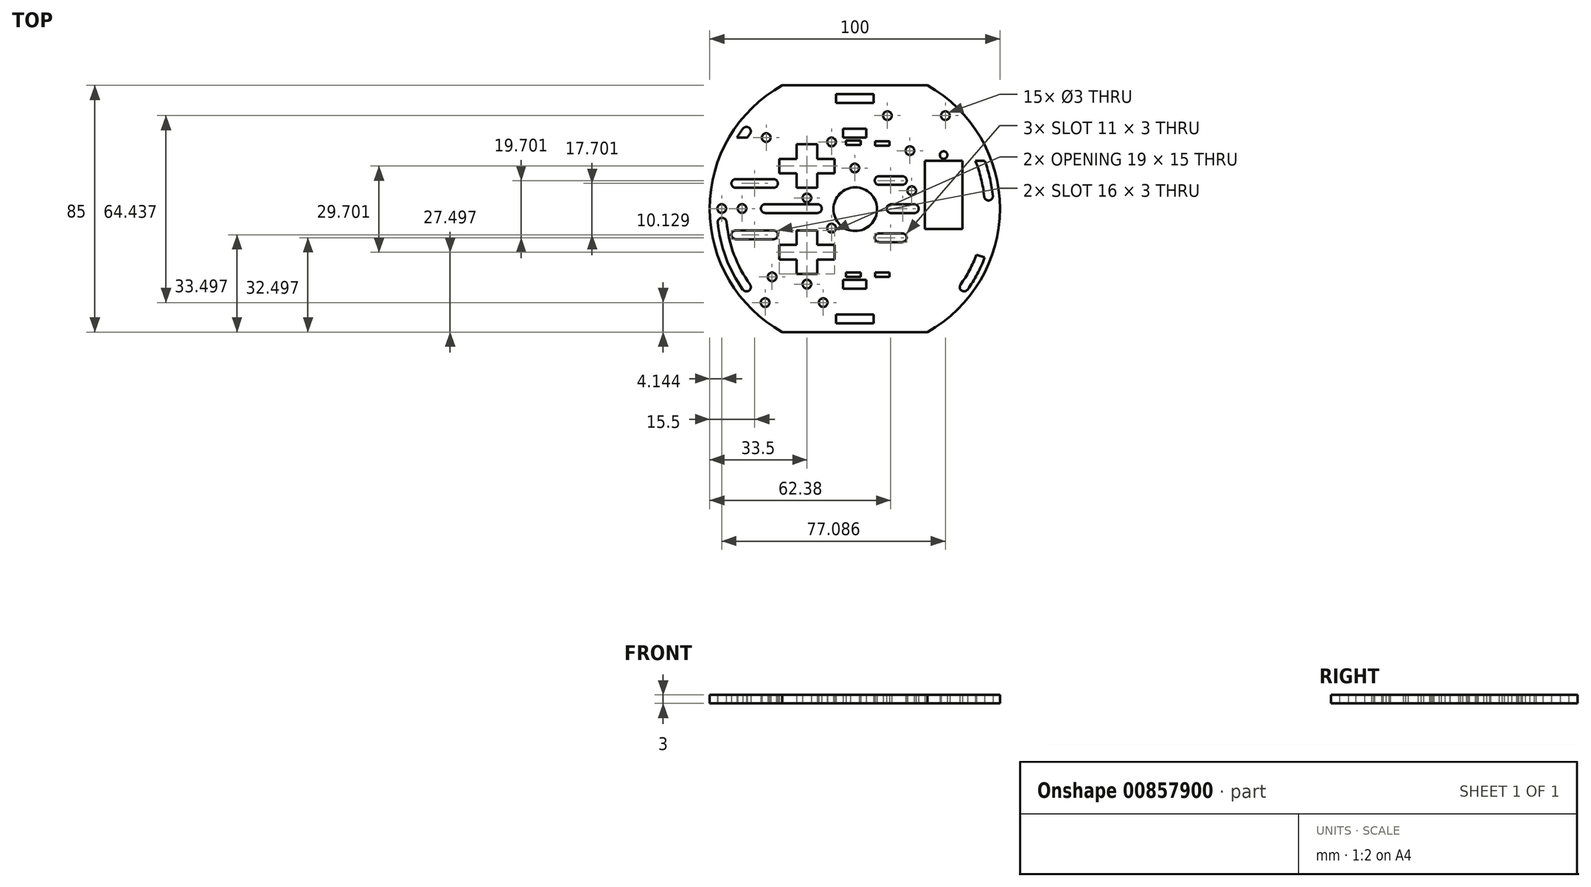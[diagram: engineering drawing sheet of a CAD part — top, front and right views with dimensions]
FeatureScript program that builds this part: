
annotation { "Feature Type Name" : "Feature", "Feature Type Description" : "" }
export const myFeature = defineFeature(function(context is Context, id is Id, definition is map)
    precondition{}
    {
        {
            var Q0;
            Q0=qCreatedBy(makeId("Top.planeOp"),FACE);
            var sketch = newSketch(context, id + "F0", { "sketchPlane" : qUnion([Q0])});
            skLineSegment(sketch, "E0", {"start": v(0, 43.49) * mm, "end": v(0, -41.51) * mm});
            skLineSegment(sketch, "E1.MirrorCS", {"start": v(0, -41.51) * mm, "end": v(25, -41.51) * mm});
            skLineSegment(sketch, "E2.MirrorCS", {"start": v(0, -41.51) * mm, "end": v(-25, -41.51) * mm});
            skLineSegment(sketch, "E3.MirrorCS", {"start": v(0, 43.49) * mm, "end": v(-25, 43.49) * mm});
            skLineSegment(sketch, "E4.MirrorCS", {"start": v(0, 43.49) * mm, "end": v(25, 43.49) * mm});
            skLineSegment(sketch, "E5", {"start": v(-50, 0.99) * mm, "end": v(0, 0.99) * mm});
            skPoint(sketch, "E5.startSnap0", {"position": v(0, 0.99) * mm});
            skLineSegment(sketch, "E6.MirrorCS", {"start": v(50, 0.99) * mm, "end": v(0, 0.99) * mm});
            skArc(sketch, "E7", {"start": v(-25, 43.49) * mm, "mid": v(-50, 0.99) * mm, "end": v(-25, -41.51) * mm});
            skArc(sketch, "E8.MirrorCS", {"start": v(25, 43.49) * mm, "mid": v(50, 0.99) * mm, "end": v(25, -41.51) * mm});
            skSolve(sketch);
        }
        {
            var Q0;
            {var subQ0=sQuery(id+"F0.wireOp",EDGE,"E4.MirrorCS");Q0=makeQuery(id+"F0.imprint","IMPRINT",FACE,{"disambiguationData":[TD([[makeQuery(id+"F0.imprint","IMPRINT",EDGE,{"derivedFrom":subQ0}),-1.0]])]});}
            var Q1;
            {var subQ0=sQuery(id+"F0.wireOp",EDGE,"E3.MirrorCS");Q1=makeQuery(id+"F0.imprint","IMPRINT",FACE,{"disambiguationData":[TD([[makeQuery(id+"F0.imprint","IMPRINT",EDGE,{"derivedFrom":subQ0}),1.0]])]});}
            var Q2;
            {var subQ0=sQuery(id+"F0.wireOp",EDGE,"E2.MirrorCS");Q2=makeQuery(id+"F0.imprint","IMPRINT",FACE,{"disambiguationData":[TD([[makeQuery(id+"F0.imprint","IMPRINT",EDGE,{"derivedFrom":subQ0}),-1.0]])]});}
            var Q3;
            {var subQ0=sQuery(id+"F0.wireOp",EDGE,"E1.MirrorCS");Q3=makeQuery(id+"F0.imprint","IMPRINT",FACE,{"disambiguationData":[TD([[makeQuery(id+"F0.imprint","IMPRINT",EDGE,{"derivedFrom":subQ0}),1.0]])]});}
            extrude(context, id + "F1", {"entities" : qUnion([Q0, Q1, Q2, Q3]), "depth" : 3 * mm, "offsetDistance" : 25.4 * mm});
        }
        {
            var Q0;
            Q0=qCreatedBy(makeId("Top.planeOp"),FACE);
            var sketch = newSketch(context, id + "F2", { "sketchPlane" : qUnion([Q0])});
            skLineSegment(sketch, "E9", {"start": v(-6.5, -38.51) * mm, "end": v(-6.5, -35.51) * mm});
            skLineSegment(sketch, "E10", {"start": v(-6.5, -35.51) * mm, "end": v(6.5, -35.51) * mm});
            skLineSegment(sketch, "E11", {"start": v(6.5, -35.51) * mm, "end": v(6.5, -38.51) * mm});
            skLineSegment(sketch, "E12", {"start": v(-6.5, -38.51) * mm, "end": v(6.5, -38.51) * mm});
            skCircle(sketch, "E13", {"center": v(0.17, 0.84) * mm, "radius": 7.5 * mm});
            skLineSegment(sketch, "E14", {"start": v(0, -26.51) * mm, "end": v(-4, -26.51) * mm});
            skLineSegment(sketch, "E15.MirrorCS", {"start": v(0, -26.51) * mm, "end": v(4, -26.51) * mm});
            skLineSegment(sketch, "E16", {"start": v(-4, -26.51) * mm, "end": v(-4, -23.51) * mm});
            skLineSegment(sketch, "E17", {"start": v(-4, -23.51) * mm, "end": v(4, -23.51) * mm});
            skLineSegment(sketch, "E18", {"start": v(4, -23.51) * mm, "end": v(4, -26.51) * mm});
            skLineSegment(sketch, "E19", {"start": v(-3, -22.51) * mm, "end": v(2, -22.51) * mm});
            skLineSegment(sketch, "E20", {"start": v(2, -22.51) * mm, "end": v(2, -21.01) * mm});
            skLineSegment(sketch, "E21", {"start": v(-3, -22.51) * mm, "end": v(-3, -21.01) * mm});
            skLineSegment(sketch, "E22", {"start": v(-3, -21.01) * mm, "end": v(2, -21.01) * mm});
            skLineSegment(sketch, "E23", {"start": v(37.11, 17.49) * mm, "end": v(37.11, -6.01) * mm});
            skLineSegment(sketch, "E24.MirrorCS", {"start": v(-6.5, 40.49) * mm, "end": v(6.5, 40.49) * mm});
            skLineSegment(sketch, "E25.MirrorCS", {"start": v(-6.5, 37.49) * mm, "end": v(6.5, 37.49) * mm});
            skLineSegment(sketch, "E26.MirrorCS", {"start": v(-6.5, 40.49) * mm, "end": v(-6.5, 37.49) * mm});
            skLineSegment(sketch, "E27.MirrorCS", {"start": v(6.5, 37.49) * mm, "end": v(6.5, 40.49) * mm});
            skLineSegment(sketch, "E28.MirrorCS", {"start": v(0, 28.49) * mm, "end": v(4, 28.49) * mm});
            skLineSegment(sketch, "E29.MirrorCS", {"start": v(0, 28.49) * mm, "end": v(-4, 28.49) * mm});
            skLineSegment(sketch, "E30.MirrorCS", {"start": v(-4, 28.49) * mm, "end": v(-4, 25.49) * mm});
            skLineSegment(sketch, "E31.MirrorCS", {"start": v(4, 25.49) * mm, "end": v(4, 28.49) * mm});
            skLineSegment(sketch, "E32.MirrorCS", {"start": v(-4, 25.49) * mm, "end": v(4, 25.49) * mm});
            skLineSegment(sketch, "E33.MirrorCS", {"start": v(-3, 24.49) * mm, "end": v(2, 24.49) * mm});
            skLineSegment(sketch, "E34.MirrorCS", {"start": v(-3, 24.49) * mm, "end": v(-3, 22.99) * mm});
            skLineSegment(sketch, "E35.MirrorCS", {"start": v(-3, 22.99) * mm, "end": v(2, 22.99) * mm});
            skLineSegment(sketch, "E36.MirrorCS", {"start": v(2, 24.49) * mm, "end": v(2, 22.99) * mm});
            skLineSegment(sketch, "E37", {"start": v(0, 43.49) * mm, "end": v(0, 40.49) * mm});
            skLineSegment(sketch, "E38", {"start": v(7, -21.01) * mm, "end": v(7, -22.51) * mm});
            skLineSegment(sketch, "E39", {"start": v(7, -21.01) * mm, "end": v(12, -21.01) * mm});
            skLineSegment(sketch, "E40", {"start": v(12, -21.01) * mm, "end": v(12, -22.51) * mm});
            skLineSegment(sketch, "E41", {"start": v(7, -22.51) * mm, "end": v(12, -22.51) * mm});
            skLineSegment(sketch, "E42", {"start": v(0.17, 0.84) * mm, "end": v(3.4, 0.84) * mm});
            skLineSegment(sketch, "E43.MirrorCS", {"start": v(7, 24.19) * mm, "end": v(12, 24.19) * mm});
            skLineSegment(sketch, "E44.MirrorCS", {"start": v(7, 22.69) * mm, "end": v(12, 22.69) * mm});
            skLineSegment(sketch, "E45.MirrorCS", {"start": v(7, 22.69) * mm, "end": v(7, 24.19) * mm});
            skLineSegment(sketch, "E46.MirrorCS", {"start": v(12, 22.69) * mm, "end": v(12, 24.19) * mm});
            skLineSegment(sketch, "E47", {"start": v(-25, -41.51) * mm, "end": v(-22, -41.51) * mm});
            skLineSegment(sketch, "E48", {"start": v(-20, -21.51) * mm, "end": v(-13, -21.51) * mm});
            skLineSegment(sketch, "E49", {"start": v(-20, -21.51) * mm, "end": v(-20, -16.51) * mm});
            skLineSegment(sketch, "E50", {"start": v(-20, -16.51) * mm, "end": v(-26, -16.51) * mm});
            skLineSegment(sketch, "E51", {"start": v(-26, -16.51) * mm, "end": v(-26, -11.51) * mm});
            skLineSegment(sketch, "E52", {"start": v(-26, -11.51) * mm, "end": v(-20, -11.51) * mm});
            skLineSegment(sketch, "E53", {"start": v(-20, -11.51) * mm, "end": v(-20, -6.51) * mm});
            skLineSegment(sketch, "E54", {"start": v(-20, -6.51) * mm, "end": v(-13, -6.51) * mm});
            skLineSegment(sketch, "E55", {"start": v(-13, -6.51) * mm, "end": v(-13, -11.51) * mm});
            skLineSegment(sketch, "E56", {"start": v(-13, -11.51) * mm, "end": v(-7, -11.51) * mm});
            skLineSegment(sketch, "E57", {"start": v(-7, -11.51) * mm, "end": v(-7, -16.51) * mm});
            skLineSegment(sketch, "E58", {"start": v(-7, -16.51) * mm, "end": v(-13, -16.51) * mm});
            skLineSegment(sketch, "E59", {"start": v(-13, -21.51) * mm, "end": v(-13, -16.51) * mm});
            skLineSegment(sketch, "E60.MirrorCS", {"start": v(-26, 13.19) * mm, "end": v(-20, 13.19) * mm});
            skLineSegment(sketch, "E61.MirrorCS", {"start": v(-26, 18.19) * mm, "end": v(-26, 13.19) * mm});
            skLineSegment(sketch, "E62.MirrorCS", {"start": v(-20, 18.19) * mm, "end": v(-26, 18.19) * mm});
            skLineSegment(sketch, "E63.MirrorCS", {"start": v(-20, 23.19) * mm, "end": v(-20, 18.19) * mm});
            skLineSegment(sketch, "E64.MirrorCS", {"start": v(-20, 23.19) * mm, "end": v(-13, 23.19) * mm});
            skLineSegment(sketch, "E65.MirrorCS", {"start": v(-13, 23.19) * mm, "end": v(-13, 18.19) * mm});
            skLineSegment(sketch, "E66.MirrorCS", {"start": v(-7, 18.19) * mm, "end": v(-13, 18.19) * mm});
            skLineSegment(sketch, "E67.MirrorCS", {"start": v(-7, 13.19) * mm, "end": v(-7, 18.19) * mm});
            skLineSegment(sketch, "E68.MirrorCS", {"start": v(-13, 13.19) * mm, "end": v(-7, 13.19) * mm});
            skLineSegment(sketch, "E69.MirrorCS", {"start": v(-13, 8.19) * mm, "end": v(-13, 13.19) * mm});
            skLineSegment(sketch, "E70.MirrorCS", {"start": v(-20, 8.19) * mm, "end": v(-13, 8.19) * mm});
            skLineSegment(sketch, "E71.MirrorCS", {"start": v(-20, 13.19) * mm, "end": v(-20, 8.19) * mm});
            skLineSegment(sketch, "E72", {"start": v(-28, -9.51) * mm, "end": v(-41, -9.51) * mm});
            skLineSegment(sketch, "E73", {"start": v(-41, -6.51) * mm, "end": v(-28, -6.51) * mm});
            skArc(sketch, "E74", {"start": v(-28, -6.51) * mm, "mid": v(-26.5, -8.01) * mm, "end": v(-28, -9.51) * mm});
            skArc(sketch, "E75", {"start": v(-41, -6.51) * mm, "mid": v(-42.5, -8.01) * mm, "end": v(-41, -9.51) * mm});
            skLineSegment(sketch, "E76.MirrorCS", {"start": v(-41, 8.19) * mm, "end": v(-28, 8.19) * mm});
            skArc(sketch, "E77.MirrorCS", {"start": v(-41, 8.19) * mm, "mid": v(-42.5, 9.69) * mm, "end": v(-41, 11.19) * mm});
            skLineSegment(sketch, "E78.MirrorCS", {"start": v(-28, 11.19) * mm, "end": v(-41, 11.19) * mm});
            skArc(sketch, "E79.MirrorCS", {"start": v(-28, 8.19) * mm, "mid": v(-26.5, 9.69) * mm, "end": v(-28, 11.19) * mm});
            skLineSegment(sketch, "E80", {"start": v(16.38, 12.19) * mm, "end": v(8.38, 12.19) * mm});
            skLineSegment(sketch, "E81", {"start": v(8.38, 9.19) * mm, "end": v(16.38, 9.19) * mm});
            skArc(sketch, "E82", {"start": v(8.38, 9.19) * mm, "mid": v(6.88, 10.69) * mm, "end": v(8.38, 12.19) * mm});
            skArc(sketch, "E83", {"start": v(16.38, 9.19) * mm, "mid": v(17.88, 10.69) * mm, "end": v(16.38, 12.19) * mm});
            skArc(sketch, "E84.MirrorCS", {"start": v(8.38, -7.51) * mm, "mid": v(6.88, -9.01) * mm, "end": v(8.38, -10.51) * mm});
            skArc(sketch, "E85.MirrorCS", {"start": v(16.38, -7.51) * mm, "mid": v(17.88, -9.01) * mm, "end": v(16.38, -10.51) * mm});
            skLineSegment(sketch, "E86", {"start": v(12.38, 43.49) * mm, "end": v(4.46, 43.49) * mm});
            skLineSegment(sketch, "E87", {"start": v(12.5, 2.49) * mm, "end": v(20.5, 2.49) * mm});
            skLineSegment(sketch, "E88", {"start": v(12.5, -0.51) * mm, "end": v(20.5, -0.51) * mm});
            skArc(sketch, "E89", {"start": v(12.5, 2.49) * mm, "mid": v(11, 0.99) * mm, "end": v(12.5, -0.51) * mm});
            skArc(sketch, "E90", {"start": v(20.5, -0.51) * mm, "mid": v(22, 0.99) * mm, "end": v(20.5, 2.49) * mm});
            skLineSegment(sketch, "E91", {"start": v(-12.86, 2.52) * mm, "end": v(-30.86, 2.52) * mm});
            skLineSegment(sketch, "E92", {"start": v(-30.4, 2.52) * mm, "end": v(-30.4, -0.48) * mm});
            skLineSegment(sketch, "E93", {"start": v(-30.86, -0.48) * mm, "end": v(-12.86, -0.48) * mm});
            skArc(sketch, "E94", {"start": v(-30.86, -0.48) * mm, "mid": v(-32.36, 1.02) * mm, "end": v(-30.86, 2.52) * mm});
            skArc(sketch, "E95", {"start": v(-12.86, -0.48) * mm, "mid": v(-11.36, 1.02) * mm, "end": v(-12.86, 2.52) * mm});
            skLineSegment(sketch, "E96.MirrorCS", {"start": v(16.38, -10.51) * mm, "end": v(8.38, -10.51) * mm});
            skLineSegment(sketch, "E97.MirrorCS", {"start": v(8.38, -7.51) * mm, "end": v(16.38, -7.51) * mm});
            skLineSegment(sketch, "E98", {"start": v(37.11, 17.49) * mm, "end": v(47.11, 17.49) * mm});
            skLineSegment(sketch, "E99", {"start": v(6.5, -38.51) * mm, "end": v(6.5, -41.51) * mm});
            skLineSegment(sketch, "E100", {"start": v(6.5, -41.51) * mm, "end": v(18.19, -41.51) * mm});
            skLineSegment(sketch, "E101", {"start": v(0, -35.51) * mm, "end": v(0, -37.8) * mm});
            skLineSegment(sketch, "E102", {"start": v(-13.99, -32.34) * mm, "end": v(-13.99, -41.51) * mm});
            skLineSegment(sketch, "E103", {"start": v(-13.99, -41.51) * mm, "end": v(-8.96, -41.51) * mm});
            skLineSegment(sketch, "E104", {"start": v(-12.39, -31.38) * mm, "end": v(-12.39, -37) * mm});
            skLineSegment(sketch, "E105", {"start": v(-12.39, -37) * mm, "end": v(-9.53, -37) * mm});
            skLineSegment(sketch, "E106", {"start": v(-29.39, -31.38) * mm, "end": v(-12.39, -31.38) * mm});
            skLineSegment(sketch, "E107", {"start": v(0.17, 0.84) * mm, "end": v(0.17, 6.05) * mm});
            skLineSegment(sketch, "E108", {"start": v(-16.5, 8.19) * mm, "end": v(-16.5, 6.19) * mm});
            skLineSegment(sketch, "E109", {"start": v(-26, 15.69) * mm, "end": v(-22.04, 15.69) * mm});
            skPoint(sketch, "E109.endSnap0", {"position": v(-7, 15.69) * mm});
            skLineSegment(sketch, "E110", {"start": v(-16.5, -21.51) * mm, "end": v(-16.5, -23.51) * mm});
            skLineSegment(sketch, "E111", {"start": v(-12.39, -31.38) * mm, "end": v(-10.89, -31.38) * mm});
            skCircle(sketch, "E112", {"center": v(-10.89, -31.38) * mm, "radius": 1.5 * mm});
            skLineSegment(sketch, "E113", {"start": v(-29.39, -31.38) * mm, "end": v(-30.89, -31.38) * mm});
            skCircle(sketch, "E114", {"center": v(-30.89, -31.38) * mm, "radius": 1.5 * mm});
            skCircle(sketch, "E115.MirrorC", {"center": v(31.23, -31.38) * mm, "radius": 1.5 * mm});
            skCircle(sketch, "E116.MirrorC", {"center": v(11.23, -31.38) * mm, "radius": 1.5 * mm});
            skCircle(sketch, "E117.MirrorC", {"center": v(11.23, 33.06) * mm, "radius": 1.5 * mm});
            skCircle(sketch, "E118.MirrorC", {"center": v(31.23, 33.06) * mm, "radius": 1.5 * mm});
            skCircle(sketch, "E119.MirrorC", {"center": v(-30.89, 33.06) * mm, "radius": 1.5 * mm});
            skCircle(sketch, "E120.MirrorC", {"center": v(-10.89, 33.06) * mm, "radius": 1.5 * mm});
            skLineSegment(sketch, "E121", {"start": v(-16.5, 6.19) * mm, "end": v(-16.5, 4.69) * mm});
            skCircle(sketch, "E122", {"center": v(-16.5, 4.69) * mm, "radius": 1.5 * mm});
            skCircle(sketch, "E123.MirrorC", {"center": v(-16.5, 26.69) * mm, "radius": 1.5 * mm});
            skCircle(sketch, "E124.MirrorC", {"center": v(-16.5, -3.01) * mm, "radius": 1.5 * mm});
            skCircle(sketch, "E125.MirrorC", {"center": v(-16.5, -25.01) * mm, "radius": 1.5 * mm});
            skLineSegment(sketch, "E126", {"start": v(-32.36, 1.02) * mm, "end": v(-37.36, 1.02) * mm});
            skLineSegment(sketch, "E127", {"start": v(-37.36, 1.02) * mm, "end": v(-38.86, 1.02) * mm});
            skCircle(sketch, "E128", {"center": v(-38.86, 1.02) * mm, "radius": 1.5 * mm});
            skLineSegment(sketch, "E129", {"start": v(-40.36, 1.02) * mm, "end": v(-44.36, 1.02) * mm});
            skLineSegment(sketch, "E130", {"start": v(-44.36, 1.02) * mm, "end": v(-45.86, 1.02) * mm});
            skCircle(sketch, "E131", {"center": v(-45.86, 1.02) * mm, "radius": 1.5 * mm});
            skCircle(sketch, "E132.MirrorC", {"center": v(39.2, 1.02) * mm, "radius": 1.5 * mm});
            skCircle(sketch, "E133.MirrorC", {"center": v(46.2, 1.02) * mm, "radius": 1.5 * mm});
            skLineSegment(sketch, "E134", {"start": v(24.11, 5.74) * mm, "end": v(28.02, 5.74) * mm});
            skLineSegment(sketch, "E135", {"start": v(24.11, 17.49) * mm, "end": v(37.11, 17.49) * mm});
            skLineSegment(sketch, "E136", {"start": v(37.11, -6.01) * mm, "end": v(24.11, -6.01) * mm});
            skLineSegment(sketch, "E137", {"start": v(30.61, 17.49) * mm, "end": v(30.61, 18.49) * mm});
            skLineSegment(sketch, "E138", {"start": v(30.61, 18.49) * mm, "end": v(30.61, 19.49) * mm});
            skCircle(sketch, "E139", {"center": v(30.61, 19.49) * mm, "radius": 1.3 * mm});
            skCircle(sketch, "E140.MirrorC", {"center": v(30.61, -8.01) * mm, "radius": 1.3 * mm});
            skLineSegment(sketch, "E141", {"start": v(25, 43.49) * mm, "end": v(19, 43.49) * mm});
            skLineSegment(sketch, "E142", {"start": v(19, 43.49) * mm, "end": v(19, 22.49) * mm});
            skLineSegment(sketch, "E143", {"start": v(19, 22.49) * mm, "end": v(19, 20.99) * mm});
            skCircle(sketch, "E144", {"center": v(19, 20.99) * mm, "radius": 1.5 * mm});
            skCircle(sketch, "E145.MirrorC", {"center": v(19, -19.31) * mm, "radius": 1.5 * mm});
            skLineSegment(sketch, "E146", {"start": v(-8, 43.49) * mm, "end": v(-8, 25.49) * mm});
            skLineSegment(sketch, "E147", {"start": v(-8, 25.49) * mm, "end": v(-8, 23.99) * mm});
            skCircle(sketch, "E148", {"center": v(-8, 23.99) * mm, "radius": 1.5 * mm});
            skCircle(sketch, "E149.MirrorC", {"center": v(-8, 7.39) * mm, "radius": 1.5 * mm});
            skCircle(sketch, "E150.MirrorC", {"center": v(-8, -5.71) * mm, "radius": 1.5 * mm});
            skCircle(sketch, "E151.MirrorC", {"center": v(-8, -22.31) * mm, "radius": 1.5 * mm});
            skLineSegment(sketch, "E152", {"start": v(25, 43.49) * mm, "end": v(0, 43.49) * mm});
            skLineSegment(sketch, "E153", {"start": v(0, 43.49) * mm, "end": v(0, 16.49) * mm});
            skLineSegment(sketch, "E154", {"start": v(0, 16.49) * mm, "end": v(0, 14.99) * mm});
            skCircle(sketch, "E155", {"center": v(0, 14.99) * mm, "radius": 1.5 * mm});
            skCircle(sketch, "E156.MirrorC", {"center": v(0, -13.31) * mm, "radius": 1.5 * mm});
            skLineSegment(sketch, "E157", {"start": v(-25, 43.49) * mm, "end": v(-21, 43.49) * mm});
            skLineSegment(sketch, "E158", {"start": v(-21, 43.49) * mm, "end": v(-21, 25.49) * mm});
            skLineSegment(sketch, "E159", {"start": v(-21, 25.49) * mm, "end": v(-29, 25.49) * mm});
            skLineSegment(sketch, "E160", {"start": v(-29, 25.49) * mm, "end": v(-30.5, 25.49) * mm});
            skCircle(sketch, "E161", {"center": v(-30.5, 25.49) * mm, "radius": 1.5 * mm});
            skLineSegment(sketch, "E162", {"start": v(-32, 25.49) * mm, "end": v(-43.38, 25.49) * mm});
            skLineSegment(sketch, "E163", {"start": v(-22, -41.51) * mm, "end": v(-22, -22.51) * mm});
            skLineSegment(sketch, "E164", {"start": v(-22, -22.51) * mm, "end": v(-27, -22.51) * mm});
            skLineSegment(sketch, "E165", {"start": v(-27, -22.51) * mm, "end": v(-28.5, -22.51) * mm});
            skCircle(sketch, "E166", {"center": v(-28.5, -22.51) * mm, "radius": 1.5 * mm});
            skLineSegment(sketch, "E167", {"start": v(24.11, 7.19) * mm, "end": v(21.11, 7.19) * mm});
            skLineSegment(sketch, "E168", {"start": v(21.11, 7.19) * mm, "end": v(19.61, 7.19) * mm});
            skCircle(sketch, "E169", {"center": v(19.61, 7.19) * mm, "radius": 1.5 * mm});
            skLineSegment(sketch, "E170", {"start": v(24.11, 17.49) * mm, "end": v(24.11, -6.01) * mm});
            skCircle(sketch, "E171.MirrorC", {"center": v(19.61, -5.51) * mm, "radius": 1.5 * mm});
            skArc(sketch, "E172", {"start": v(47.59, -3.52) * mm, "mid": v(44.79, -15.8) * mm, "end": v(38.88, -26.9) * mm});
            skArc(sketch, "E173", {"start": v(44.58, -3.52) * mm, "mid": v(41.94, -14.87) * mm, "end": v(36.45, -25.14) * mm});
            skArc(sketch, "E174", {"start": v(36.45, -25.14) * mm, "mid": v(36.79, -27.22) * mm, "end": v(38.88, -26.9) * mm});
            skArc(sketch, "E175", {"start": v(44.58, -3.52) * mm, "mid": v(46.08, -2.16) * mm, "end": v(47.59, -3.52) * mm});
            skLineSegment(sketch, "E176", {"start": v(41.94, -14.87) * mm, "end": v(44.79, -15.8) * mm});
            skArc(sketch, "E177.MirrorCS", {"start": v(-47.25, -3.52) * mm, "mid": v(-44.45, -15.8) * mm, "end": v(-38.53, -26.9) * mm});
            skArc(sketch, "E178.MirrorCS", {"start": v(-44.23, -3.52) * mm, "mid": v(-41.6, -14.87) * mm, "end": v(-36.1, -25.14) * mm});
            skArc(sketch, "E179.MirrorCS", {"start": v(-36.1, -25.14) * mm, "mid": v(-36.45, -27.22) * mm, "end": v(-38.53, -26.9) * mm});
            skArc(sketch, "E180.MirrorCS", {"start": v(-44.23, -3.52) * mm, "mid": v(-45.74, -2.16) * mm, "end": v(-47.25, -3.52) * mm});
            skArc(sketch, "E181.MirrorCS", {"start": v(44.58, 5.2) * mm, "mid": v(41.94, 16.54) * mm, "end": v(36.45, 26.81) * mm});
            skArc(sketch, "E182.MirrorCS", {"start": v(47.59, 5.2) * mm, "mid": v(44.79, 17.47) * mm, "end": v(38.88, 28.57) * mm});
            skArc(sketch, "E183.MirrorCS", {"start": v(44.58, 5.2) * mm, "mid": v(46.08, 3.83) * mm, "end": v(47.59, 5.2) * mm});
            skArc(sketch, "E184.MirrorCS", {"start": v(36.45, 26.81) * mm, "mid": v(36.79, 28.9) * mm, "end": v(38.88, 28.57) * mm});
            skArc(sketch, "E185.MirrorCS", {"start": v(-47.25, 5.2) * mm, "mid": v(-44.45, 17.47) * mm, "end": v(-38.53, 28.57) * mm});
            skArc(sketch, "E186.MirrorCS", {"start": v(-44.23, 5.2) * mm, "mid": v(-41.6, 16.54) * mm, "end": v(-36.1, 26.81) * mm});
            skArc(sketch, "E187.MirrorCS", {"start": v(-36.1, 26.81) * mm, "mid": v(-36.45, 28.9) * mm, "end": v(-38.53, 28.57) * mm});
            skArc(sketch, "E188.MirrorCS", {"start": v(-44.23, 5.2) * mm, "mid": v(-45.74, 3.83) * mm, "end": v(-47.25, 5.2) * mm});
            skSolve(sketch);
        }
        {
            var Q0;
            Q0=makeQuery(id+"F2.imprint","IMPRINT",FACE,{"disambiguationData":[TD([[makeQuery(id+"F2.imprint","IMPRINT",EDGE,{"derivedFrom":sQuery(id+"F2.wireOp",EDGE,"2JhbG11d-Ylxn-ed14-tFHQ-MPQ8VMmL4TC8")}),1.0]])]});
            var Q1;
            Q1=makeQuery(id+"F2.imprint","IMPRINT",FACE,{"disambiguationData":[TD([[makeQuery(id+"F2.imprint","IMPRINT",EDGE,{"derivedFrom":sQuery(id+"F2.wireOp",EDGE,"E13")}),1.0]])]});
            var Q2;
            Q2=makeQuery(id+"F2.imprint","IMPRINT",FACE,{"disambiguationData":[TD([[makeQuery(id+"F2.imprint","IMPRINT",EDGE,{"derivedFrom":sQuery(id+"F2.wireOp",EDGE,"E60.MirrorCS")}),1.0]])]});
            var Q3;
            Q3=makeQuery(id+"F2.imprint","IMPRINT",FACE,{"disambiguationData":[TD([[makeQuery(id+"F2.imprint","IMPRINT",EDGE,{"derivedFrom":sQuery(id+"F2.wireOp",EDGE,"E25.MirrorCS")}),1.0]])]});
            var Q4;
            Q4=makeQuery(id+"F2.imprint","IMPRINT",FACE,{"disambiguationData":[TD([[makeQuery(id+"F2.imprint","IMPRINT",EDGE,{"derivedFrom":sQuery(id+"F2.wireOp",EDGE,"E48")}),1.0]])]});
            var Q5;
            Q5=makeQuery(id+"F2.imprint","IMPRINT",FACE,{"disambiguationData":[TD([[makeQuery(id+"F2.imprint","IMPRINT",EDGE,{"derivedFrom":sQuery(id+"F2.wireOp",EDGE,"E19")}),1.0]])]});
            extrude(context, id + "F3", {"entities" : qUnion([Q0, Q1, Q2, Q3, Q4, Q5]), "operationType" : NewBodyOperationType.REMOVE, "oppositeDirection" : true, "depth" : 25.4 * mm, "offsetDistance" : 25.4 * mm});
        }
        {
            var Q0;
            Q0=makeQuery(id+"F2.imprint","IMPRINT",FACE,{"disambiguationData":[TD([[makeQuery(id+"F2.imprint","IMPRINT",EDGE,{"derivedFrom":sQuery(id+"F2.wireOp",EDGE,"E28.MirrorCS")}),-1.0]])]});
            var Q1;
            Q1=makeQuery(id+"F2.imprint","IMPRINT",FACE,{"disambiguationData":[TD([[makeQuery(id+"F2.imprint","IMPRINT",EDGE,{"derivedFrom":sQuery(id+"F2.wireOp",EDGE,"E19")}),1.0]])]});
            var Q2;
            Q2=makeQuery(id+"F2.imprint","IMPRINT",FACE,{"disambiguationData":[TD([[makeQuery(id+"F2.imprint","IMPRINT",EDGE,{"derivedFrom":sQuery(id+"F2.wireOp",EDGE,"E38")}),1.0]])]});
            var Q3;
            Q3=makeQuery(id+"F2.imprint","IMPRINT",FACE,{"disambiguationData":[TD([[makeQuery(id+"F2.imprint","IMPRINT",EDGE,{"derivedFrom":sQuery(id+"F2.wireOp",EDGE,"E9")}),-1.0]])]});
            var Q4;
            Q4=makeQuery(id+"F2.imprint","IMPRINT",FACE,{"disambiguationData":[TD([[makeQuery(id+"F2.imprint","IMPRINT",EDGE,{"derivedFrom":sQuery(id+"F2.wireOp",EDGE,"E33.MirrorCS")}),-1.0]])]});
            var Q5;
            Q5=makeQuery(id+"F2.imprint","IMPRINT",FACE,{"disambiguationData":[TD([[makeQuery(id+"F2.imprint","IMPRINT",EDGE,{"derivedFrom":sQuery(id+"F2.wireOp",EDGE,"E14")}),-1.0]])]});
            var Q6;
            Q6=makeQuery(id+"F2.imprint","IMPRINT",FACE,{"disambiguationData":[TD([[makeQuery(id+"F2.imprint","IMPRINT",EDGE,{"derivedFrom":sQuery(id+"F2.wireOp",EDGE,"E43.MirrorCS")}),-1.0]])]});
            extrude(context, id + "F4", {"entities" : qUnion([Q0, Q1, Q2, Q3, Q4, Q5, Q6]), "operationType" : NewBodyOperationType.REMOVE, "oppositeDirection" : true, "depth" : 25.4 * mm, "offsetDistance" : 25.4 * mm});
        }
        {
            var Q0;
            Q0=makeQuery(id+"F2.imprint","IMPRINT",FACE,{"disambiguationData":[TD([[makeQuery(id+"F2.imprint","IMPRINT",EDGE,{"derivedFrom":sQuery(id+"F2.wireOp",EDGE,"E177.MirrorCS")}),1.0]])]});
            var Q1;
            {var subQ0=sQuery(id+"F2.wireOp",EDGE,"E128");var subQ1=makeQuery(id+"F2.imprint","IMPRINT",VERTEX,{"disambiguationData":[OD(0.0)],"derivedFrom":subQ0});Q1=makeQuery(id+"F2.imprint","IMPRINT",FACE,{"disambiguationData":[TD([[makeQuery(id+"F2.imprint","IMPRINT",EDGE,{"disambiguationData":[TD([[subQ1,-1.0]])],"derivedFrom":subQ0}),1.0]])]});}
            var Q2;
            Q2=makeQuery(id+"F2.imprint","IMPRINT",FACE,{"disambiguationData":[TD([[makeQuery(id+"F2.imprint","IMPRINT",EDGE,{"derivedFrom":sQuery(id+"F2.wireOp",EDGE,"E122")}),1.0]])]});
            var Q3;
            Q3=makeQuery(id+"F2.imprint","IMPRINT",FACE,{"disambiguationData":[TD([[makeQuery(id+"F2.imprint","IMPRINT",EDGE,{"derivedFrom":sQuery(id+"F2.wireOp",EDGE,"E144")}),1.0]])]});
            extrude(context, id + "F5", {"entities" : qUnion([Q0, Q1, Q2, Q3]), "operationType" : NewBodyOperationType.REMOVE, "oppositeDirection" : true, "depth" : 25.4 * mm, "offsetDistance" : 25.4 * mm});
        }
        {
            var Q0;
            {var subQ0=sQuery(id+"F2.wireOp",EDGE,"E174");Q0=makeQuery(id+"F2.imprint","IMPRINT",FACE,{"disambiguationData":[TD([[makeQuery(id+"F2.imprint","IMPRINT",EDGE,{"derivedFrom":subQ0}),1.0]])]});}
            var Q1;
            {var subQ0=sQuery(id+"F2.wireOp",EDGE,"E175");Q1=makeQuery(id+"F2.imprint","IMPRINT",FACE,{"disambiguationData":[TD([[makeQuery(id+"F2.imprint","IMPRINT",EDGE,{"derivedFrom":subQ0}),-1.0]])]});}
            extrude(context, id + "F6", {"entities" : qUnion([Q0, Q1]), "operationType" : NewBodyOperationType.REMOVE, "oppositeDirection" : true, "depth" : 25.4 * mm, "offsetDistance" : 25.4 * mm});
        }
        {
            var Q0;
            {var subQ2=sQuery(id+"F2.wireOp",EDGE,"E23");Q0=makeQuery(id+"F2.imprint","IMPRINT",FACE,{"disambiguationData":[TD([[makeQuery(id+"F2.imprint","IMPRINT",EDGE,{"derivedFrom":subQ2}),-1.0]])]});}
            var Q1;
            Q1=makeQuery(id+"F2.imprint","IMPRINT",FACE,{"disambiguationData":[TD([[makeQuery(id+"F2.imprint","IMPRINT",EDGE,{"derivedFrom":sQuery(id+"F2.wireOp",EDGE,"E13")}),1.0]])]});
            var Q2;
            {var subQ2=sQuery(id+"F2.wireOp",EDGE,"E92");Q2=makeQuery(id+"F2.imprint","IMPRINT",FACE,{"disambiguationData":[TD([[makeQuery(id+"F2.imprint","IMPRINT",EDGE,{"derivedFrom":subQ2}),1.0]])]});}
            var Q3;
            {var subQ0=sQuery(id+"F2.wireOp",EDGE,"E60.MirrorCS");Q3=makeQuery(id+"F2.imprint","IMPRINT",FACE,{"disambiguationData":[TD([[makeQuery(id+"F2.imprint","IMPRINT",EDGE,{"derivedFrom":subQ0}),1.0]])]});}
            var Q4;
            Q4=makeQuery(id+"F2.imprint","IMPRINT",FACE,{"disambiguationData":[TD([[makeQuery(id+"F2.imprint","IMPRINT",EDGE,{"derivedFrom":sQuery(id+"F2.wireOp",EDGE,"E76.MirrorCS")}),1.0]])]});
            var Q5;
            {var subQ0=sQuery(id+"F2.wireOp",EDGE,"E174");Q5=makeQuery(id+"F2.imprint","IMPRINT",FACE,{"disambiguationData":[TD([[makeQuery(id+"F2.imprint","IMPRINT",EDGE,{"derivedFrom":subQ0}),1.0]])]});}
            var Q6;
            {var subQ0=sQuery(id+"F2.wireOp",EDGE,"E175");Q6=makeQuery(id+"F2.imprint","IMPRINT",FACE,{"disambiguationData":[TD([[makeQuery(id+"F2.imprint","IMPRINT",EDGE,{"derivedFrom":subQ0}),-1.0]])]});}
            var Q7;
            Q7=makeQuery(id+"F2.imprint","IMPRINT",FACE,{"disambiguationData":[TD([[makeQuery(id+"F2.imprint","IMPRINT",EDGE,{"derivedFrom":sQuery(id+"F2.wireOp",EDGE,"E133.MirrorC")}),-1.0]])]});
            var Q8;
            Q8=makeQuery(id+"F2.imprint","IMPRINT",FACE,{"disambiguationData":[TD([[makeQuery(id+"F2.imprint","IMPRINT",EDGE,{"derivedFrom":sQuery(id+"F2.wireOp",EDGE,"E132.MirrorC")}),-1.0]])]});
            var Q9;
            {var subQ5=sQuery(id+"F2.wireOp",EDGE,"E183.MirrorCS");Q9=makeQuery(id+"F2.imprint","IMPRINT",FACE,{"disambiguationData":[TD([[makeQuery(id+"F2.imprint","IMPRINT",EDGE,{"derivedFrom":subQ5}),1.0]])]});}
            var Q10;
            {var subQ5=sQuery(id+"F2.wireOp",EDGE,"E184.MirrorCS");Q10=makeQuery(id+"F2.imprint","IMPRINT",FACE,{"disambiguationData":[TD([[makeQuery(id+"F2.imprint","IMPRINT",EDGE,{"derivedFrom":subQ5}),-1.0]])]});}
            var Q11;
            Q11=makeQuery(id+"F2.imprint","IMPRINT",FACE,{"disambiguationData":[TD([[makeQuery(id+"F2.imprint","IMPRINT",EDGE,{"derivedFrom":sQuery(id+"F2.wireOp",EDGE,"E140.MirrorC")}),-1.0]])]});
            var Q12;
            Q12=makeQuery(id+"F2.imprint","IMPRINT",FACE,{"disambiguationData":[TD([[makeQuery(id+"F2.imprint","IMPRINT",EDGE,{"derivedFrom":sQuery(id+"F2.wireOp",EDGE,"E139")}),1.0]])]});
            var Q13;
            Q13=makeQuery(id+"F2.imprint","IMPRINT",FACE,{"disambiguationData":[TD([[makeQuery(id+"F2.imprint","IMPRINT",EDGE,{"derivedFrom":sQuery(id+"F2.wireOp",EDGE,"E171.MirrorC")}),-1.0]])]});
            var Q14;
            Q14=makeQuery(id+"F2.imprint","IMPRINT",FACE,{"disambiguationData":[TD([[makeQuery(id+"F2.imprint","IMPRINT",EDGE,{"derivedFrom":sQuery(id+"F2.wireOp",EDGE,"E145.MirrorC")}),-1.0]])]});
            var Q15;
            Q15=makeQuery(id+"F2.imprint","IMPRINT",FACE,{"disambiguationData":[TD([[makeQuery(id+"F2.imprint","IMPRINT",EDGE,{"derivedFrom":sQuery(id+"F2.wireOp",EDGE,"E115.MirrorC")}),-1.0]])]});
            var Q16;
            Q16=makeQuery(id+"F2.imprint","IMPRINT",FACE,{"disambiguationData":[TD([[makeQuery(id+"F2.imprint","IMPRINT",EDGE,{"derivedFrom":sQuery(id+"F2.wireOp",EDGE,"E116.MirrorC")}),-1.0]])]});
            var Q17;
            Q17=makeQuery(id+"F2.imprint","IMPRINT",FACE,{"disambiguationData":[TD([[makeQuery(id+"F2.imprint","IMPRINT",EDGE,{"derivedFrom":sQuery(id+"F2.wireOp",EDGE,"E112")}),1.0]])]});
            var Q18;
            Q18=makeQuery(id+"F2.imprint","IMPRINT",FACE,{"disambiguationData":[TD([[makeQuery(id+"F2.imprint","IMPRINT",EDGE,{"derivedFrom":sQuery(id+"F2.wireOp",EDGE,"E125.MirrorC")}),1.0]])]});
            var Q19;
            Q19=makeQuery(id+"F2.imprint","IMPRINT",FACE,{"disambiguationData":[TD([[makeQuery(id+"F2.imprint","IMPRINT",EDGE,{"derivedFrom":sQuery(id+"F2.wireOp",EDGE,"E151.MirrorC")}),-1.0]])]});
            var Q20;
            Q20=makeQuery(id+"F2.imprint","IMPRINT",FACE,{"disambiguationData":[TD([[makeQuery(id+"F2.imprint","IMPRINT",EDGE,{"derivedFrom":sQuery(id+"F2.wireOp",EDGE,"E14")}),-1.0]])]});
            var Q21;
            Q21=makeQuery(id+"F2.imprint","IMPRINT",FACE,{"disambiguationData":[TD([[makeQuery(id+"F2.imprint","IMPRINT",EDGE,{"derivedFrom":sQuery(id+"F2.wireOp",EDGE,"E19")}),1.0]])]});
            var Q22;
            Q22=makeQuery(id+"F2.imprint","IMPRINT",FACE,{"disambiguationData":[TD([[makeQuery(id+"F2.imprint","IMPRINT",EDGE,{"derivedFrom":sQuery(id+"F2.wireOp",EDGE,"E38")}),1.0]])]});
            var Q23;
            {var subQ0=sQuery(id+"F2.wireOp",EDGE,"E49");Q23=makeQuery(id+"F2.imprint","IMPRINT",FACE,{"disambiguationData":[TD([[makeQuery(id+"F2.imprint","IMPRINT",EDGE,{"derivedFrom":subQ0}),-1.0]])]});}
            var Q24;
            Q24=makeQuery(id+"F2.imprint","IMPRINT",FACE,{"disambiguationData":[TD([[makeQuery(id+"F2.imprint","IMPRINT",EDGE,{"derivedFrom":sQuery(id+"F2.wireOp",EDGE,"E156.MirrorC")}),-1.0]])]});
            var Q25;
            Q25=makeQuery(id+"F2.imprint","IMPRINT",FACE,{"disambiguationData":[TD([[makeQuery(id+"F2.imprint","IMPRINT",EDGE,{"derivedFrom":sQuery(id+"F2.wireOp",EDGE,"E84.MirrorCS")}),1.0]])]});
            var Q26;
            Q26=makeQuery(id+"F2.imprint","IMPRINT",FACE,{"disambiguationData":[TD([[makeQuery(id+"F2.imprint","IMPRINT",EDGE,{"derivedFrom":sQuery(id+"F2.wireOp",EDGE,"E87")}),-1.0]])]});
            var Q27;
            Q27=makeQuery(id+"F2.imprint","IMPRINT",FACE,{"disambiguationData":[TD([[makeQuery(id+"F2.imprint","IMPRINT",EDGE,{"derivedFrom":sQuery(id+"F2.wireOp",EDGE,"E169")}),1.0]])]});
            var Q28;
            Q28=makeQuery(id+"F2.imprint","IMPRINT",FACE,{"disambiguationData":[TD([[makeQuery(id+"F2.imprint","IMPRINT",EDGE,{"derivedFrom":sQuery(id+"F2.wireOp",EDGE,"E80")}),1.0]])]});
            var Q29;
            Q29=makeQuery(id+"F2.imprint","IMPRINT",FACE,{"disambiguationData":[TD([[makeQuery(id+"F2.imprint","IMPRINT",EDGE,{"derivedFrom":sQuery(id+"F2.wireOp",EDGE,"E144")}),1.0]])]});
            var Q30;
            Q30=makeQuery(id+"F2.imprint","IMPRINT",FACE,{"disambiguationData":[TD([[makeQuery(id+"F2.imprint","IMPRINT",EDGE,{"derivedFrom":sQuery(id+"F2.wireOp",EDGE,"E118.MirrorC")}),1.0]])]});
            var Q31;
            Q31=makeQuery(id+"F2.imprint","IMPRINT",FACE,{"disambiguationData":[TD([[makeQuery(id+"F2.imprint","IMPRINT",EDGE,{"derivedFrom":sQuery(id+"F2.wireOp",EDGE,"E117.MirrorC")}),1.0]])]});
            var Q32;
            {var subQ0=sQuery(id+"F2.wireOp",EDGE,"E26.MirrorCS");Q32=makeQuery(id+"F2.imprint","IMPRINT",FACE,{"disambiguationData":[TD([[makeQuery(id+"F2.imprint","IMPRINT",EDGE,{"derivedFrom":subQ0}),1.0]])]});}
            var Q33;
            {var subQ0=sQuery(id+"F2.wireOp",EDGE,"E27.MirrorCS");Q33=makeQuery(id+"F2.imprint","IMPRINT",FACE,{"disambiguationData":[TD([[makeQuery(id+"F2.imprint","IMPRINT",EDGE,{"derivedFrom":subQ0}),1.0]])]});}
            var Q34;
            {var subQ0=sQuery(id+"F2.wireOp",EDGE,"E29.MirrorCS");Q34=makeQuery(id+"F2.imprint","IMPRINT",FACE,{"disambiguationData":[TD([[makeQuery(id+"F2.imprint","IMPRINT",EDGE,{"derivedFrom":subQ0}),1.0]])]});}
            var Q35;
            {var subQ0=sQuery(id+"F2.wireOp",EDGE,"E28.MirrorCS");Q35=makeQuery(id+"F2.imprint","IMPRINT",FACE,{"disambiguationData":[TD([[makeQuery(id+"F2.imprint","IMPRINT",EDGE,{"derivedFrom":subQ0}),-1.0]])]});}
            var Q36;
            {var subQ0=sQuery(id+"F2.wireOp",EDGE,"E36.MirrorCS");Q36=makeQuery(id+"F2.imprint","IMPRINT",FACE,{"disambiguationData":[TD([[makeQuery(id+"F2.imprint","IMPRINT",EDGE,{"derivedFrom":subQ0}),-1.0]])]});}
            var Q37;
            {var subQ0=sQuery(id+"F2.wireOp",EDGE,"E34.MirrorCS");Q37=makeQuery(id+"F2.imprint","IMPRINT",FACE,{"disambiguationData":[TD([[makeQuery(id+"F2.imprint","IMPRINT",EDGE,{"derivedFrom":subQ0}),1.0]])]});}
            var Q38;
            Q38=makeQuery(id+"F2.imprint","IMPRINT",FACE,{"disambiguationData":[TD([[makeQuery(id+"F2.imprint","IMPRINT",EDGE,{"derivedFrom":sQuery(id+"F2.wireOp",EDGE,"E43.MirrorCS")}),-1.0]])]});
            var Q39;
            Q39=makeQuery(id+"F2.imprint","IMPRINT",FACE,{"disambiguationData":[TD([[makeQuery(id+"F2.imprint","IMPRINT",EDGE,{"derivedFrom":sQuery(id+"F2.wireOp",EDGE,"E148")}),1.0]])]});
            var Q40;
            Q40=makeQuery(id+"F2.imprint","IMPRINT",FACE,{"disambiguationData":[TD([[makeQuery(id+"F2.imprint","IMPRINT",EDGE,{"derivedFrom":sQuery(id+"F2.wireOp",EDGE,"E155")}),1.0]])]});
            var Q41;
            Q41=makeQuery(id+"F2.imprint","IMPRINT",FACE,{"disambiguationData":[TD([[makeQuery(id+"F2.imprint","IMPRINT",EDGE,{"derivedFrom":sQuery(id+"F2.wireOp",EDGE,"E122")}),1.0]])]});
            var Q42;
            Q42=makeQuery(id+"F2.imprint","IMPRINT",FACE,{"disambiguationData":[TD([[makeQuery(id+"F2.imprint","IMPRINT",EDGE,{"derivedFrom":sQuery(id+"F2.wireOp",EDGE,"E149.MirrorC")}),-1.0]])]});
            var Q43;
            Q43=makeQuery(id+"F2.imprint","IMPRINT",FACE,{"disambiguationData":[TD([[makeQuery(id+"F2.imprint","IMPRINT",EDGE,{"derivedFrom":sQuery(id+"F2.wireOp",EDGE,"E150.MirrorC")}),1.0]])]});
            var Q44;
            Q44=makeQuery(id+"F2.imprint","IMPRINT",FACE,{"disambiguationData":[TD([[makeQuery(id+"F2.imprint","IMPRINT",EDGE,{"derivedFrom":sQuery(id+"F2.wireOp",EDGE,"E124.MirrorC")}),-1.0]])]});
            var Q45;
            Q45=makeQuery(id+"F2.imprint","IMPRINT",FACE,{"disambiguationData":[TD([[makeQuery(id+"F2.imprint","IMPRINT",EDGE,{"derivedFrom":sQuery(id+"F2.wireOp",EDGE,"E120.MirrorC")}),-1.0]])]});
            var Q46;
            Q46=makeQuery(id+"F2.imprint","IMPRINT",FACE,{"disambiguationData":[TD([[makeQuery(id+"F2.imprint","IMPRINT",EDGE,{"derivedFrom":sQuery(id+"F2.wireOp",EDGE,"E123.MirrorC")}),-1.0]])]});
            var Q47;
            {var subQ0=sQuery(id+"F2.wireOp",EDGE,"E161");var subQ1=makeQuery(id+"F2.imprint","IMPRINT",VERTEX,{"disambiguationData":[OD(0.0)],"derivedFrom":subQ0});Q47=makeQuery(id+"F2.imprint","IMPRINT",FACE,{"disambiguationData":[TD([[makeQuery(id+"F2.imprint","IMPRINT",EDGE,{"disambiguationData":[TD([[subQ1,-1.0]])],"derivedFrom":subQ0}),1.0]])]});}
            var Q48;
            Q48=makeQuery(id+"F2.imprint","IMPRINT",FACE,{"disambiguationData":[TD([[makeQuery(id+"F2.imprint","IMPRINT",EDGE,{"derivedFrom":sQuery(id+"F2.wireOp",EDGE,"E119.MirrorC")}),-1.0]])]});
            var Q49;
            {var subQ5=sQuery(id+"F2.wireOp",EDGE,"E188.MirrorCS");Q49=makeQuery(id+"F2.imprint","IMPRINT",FACE,{"disambiguationData":[TD([[makeQuery(id+"F2.imprint","IMPRINT",EDGE,{"derivedFrom":subQ5}),-1.0]])]});}
            var Q50;
            {var subQ5=sQuery(id+"F2.wireOp",EDGE,"E187.MirrorCS");Q50=makeQuery(id+"F2.imprint","IMPRINT",FACE,{"disambiguationData":[TD([[makeQuery(id+"F2.imprint","IMPRINT",EDGE,{"derivedFrom":subQ5}),1.0]])]});}
            var Q51;
            {var subQ4=sQuery(id+"F2.wireOp",EDGE,"E92");Q51=makeQuery(id+"F2.imprint","IMPRINT",FACE,{"disambiguationData":[TD([[makeQuery(id+"F2.imprint","IMPRINT",EDGE,{"derivedFrom":subQ4}),-1.0]])]});}
            var Q52;
            {var subQ0=sQuery(id+"F2.wireOp",EDGE,"E128");var subQ1=makeQuery(id+"F2.imprint","IMPRINT",VERTEX,{"disambiguationData":[OD(0.0)],"derivedFrom":subQ0});Q52=makeQuery(id+"F2.imprint","IMPRINT",FACE,{"disambiguationData":[TD([[makeQuery(id+"F2.imprint","IMPRINT",EDGE,{"disambiguationData":[TD([[subQ1,-1.0]])],"derivedFrom":subQ0}),1.0]])]});}
            var Q53;
            Q53=makeQuery(id+"F2.imprint","IMPRINT",FACE,{"disambiguationData":[TD([[makeQuery(id+"F2.imprint","IMPRINT",EDGE,{"derivedFrom":sQuery(id+"F2.wireOp",EDGE,"E72")}),-1.0]])]});
            var Q54;
            Q54=makeQuery(id+"F2.imprint","IMPRINT",FACE,{"disambiguationData":[TD([[makeQuery(id+"F2.imprint","IMPRINT",EDGE,{"derivedFrom":sQuery(id+"F2.wireOp",EDGE,"E131")}),1.0]])]});
            var Q55;
            Q55=makeQuery(id+"F2.imprint","IMPRINT",FACE,{"disambiguationData":[TD([[makeQuery(id+"F2.imprint","IMPRINT",EDGE,{"derivedFrom":sQuery(id+"F2.wireOp",EDGE,"E114")}),1.0]])]});
            var Q56;
            Q56=makeQuery(id+"F2.imprint","IMPRINT",FACE,{"disambiguationData":[TD([[makeQuery(id+"F2.imprint","IMPRINT",EDGE,{"derivedFrom":sQuery(id+"F2.wireOp",EDGE,"E166")}),1.0]])]});
            var Q57;
            Q57=makeQuery(id+"F2.imprint","IMPRINT",FACE,{"disambiguationData":[TD([[makeQuery(id+"F2.imprint","IMPRINT",EDGE,{"derivedFrom":sQuery(id+"F2.wireOp",EDGE,"E177.MirrorCS")}),1.0]])]});
            var Q58;
            {var subQ3=sQuery(id+"F2.wireOp",EDGE,"E9");Q58=makeQuery(id+"F2.imprint","IMPRINT",FACE,{"disambiguationData":[TD([[makeQuery(id+"F2.imprint","IMPRINT",EDGE,{"derivedFrom":subQ3}),-1.0]])]});}
            extrude(context, id + "F7", {"entities" : qUnion([Q0, Q1, Q2, Q3, Q4, Q5, Q6, Q7, Q8, Q9, Q10, Q11, Q12, Q13, Q14, Q15, Q16, Q17, Q18, Q19, Q20, Q21, Q22, Q23, Q24, Q25, Q26, Q27, Q28, Q29, Q30, Q31, Q32, Q33, Q34, Q35, Q36, Q37, Q38, Q39, Q40, Q41, Q42, Q43, Q44, Q45, Q46, Q47, Q48, Q49, Q50, Q51, Q52, Q53, Q54, Q55, Q56, Q57, Q58]), "operationType" : NewBodyOperationType.REMOVE, "depth" : 102.87 * mm, "offsetDistance" : 25.4 * mm});
        }
    });
